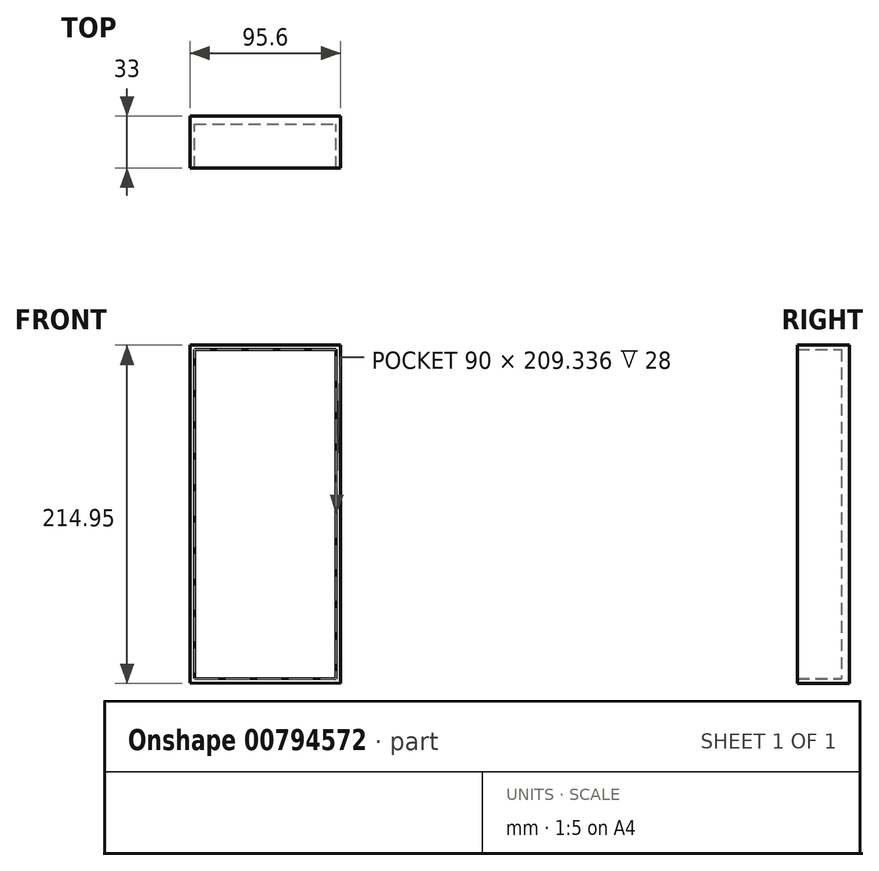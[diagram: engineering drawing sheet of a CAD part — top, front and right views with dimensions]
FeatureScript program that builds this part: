
annotation { "Feature Type Name" : "Feature", "Feature Type Description" : "" }
export const myFeature = defineFeature(function(context is Context, id is Id, definition is map)
    precondition{}
    {
        {
            var Q0;
            Q0=qCreatedBy(makeId("Front.planeOp"),FACE);
            var sketch = newSketch(context, id + "F0", { "sketchPlane" : qUnion([Q0])});
            skLineSegment(sketch, "E0", {"start": v(-49.75, 98.02) * mm, "end": v(40.25, 98.02) * mm});
            skLineSegment(sketch, "E1", {"start": v(-49.75, 98.02) * mm, "end": v(-49.75, -110.98) * mm});
            skLineSegment(sketch, "E2", {"start": v(40.25, 98.02) * mm, "end": v(40.25, -111.32) * mm});
            skLineSegment(sketch, "E3", {"start": v(-49.75, -110.98) * mm, "end": v(40.25, -111.32) * mm});
            skLineSegment(sketch, "E4.0", {"start": v(-52.55, 100.82) * mm, "end": v(43.05, 100.82) * mm});
            skLineSegment(sketch, "E4.1", {"start": v(-52.55, 100.82) * mm, "end": v(-52.55, -113.77) * mm});
            skLineSegment(sketch, "E4.2", {"start": v(-52.55, -113.77) * mm, "end": v(43.05, -114.13) * mm});
            skLineSegment(sketch, "E4.3", {"start": v(43.05, 100.82) * mm, "end": v(43.05, -114.13) * mm});
            skSolve(sketch);
        }
        {
            var Q0;
            Q0=makeQuery(id+"F0.imprint","IMPRINT",FACE,{"disambiguationData":[TD([[makeQuery(id+"F0.imprint","IMPRINT",EDGE,{"derivedFrom":sQuery(id+"F0.wireOp",EDGE,"E0")}),1.0]])]});
            extrude(context, id + "F1", {"entities" : qUnion([Q0]), "depth" : 28 * mm, "offsetDistance" : 25 * mm});
        }
        {
            var Q0;
            Q0=makeQuery(id+"F0.imprint","IMPRINT",FACE,{"disambiguationData":[TD([[makeQuery(id+"F0.imprint","IMPRINT",EDGE,{"derivedFrom":sQuery(id+"F0.wireOp",EDGE,"E0")}),-1.0]])]});
            var Q1;
            Q1=makeQuery(id+"F1.opExtrude","CAP_FACE",FACE,{"disambiguationData":[OSD([sQuery(id+"F0.wireOp",EDGE,"E0"),sQuery(id+"F0.wireOp",EDGE,"E1"),sQuery(id+"F0.wireOp",EDGE,"E2"),sQuery(id+"F0.wireOp",EDGE,"E3"),sQuery(id+"F0.wireOp",EDGE,"E4.0"),sQuery(id+"F0.wireOp",EDGE,"E4.1"),sQuery(id+"F0.wireOp",EDGE,"E4.2"),sQuery(id+"F0.wireOp",EDGE,"E4.3")])],"isStart":false});
            extrude(context, id + "F2", {"entities" : qUnion([Q0, Q1]), "operationType" : NewBodyOperationType.ADD, "depth" : 5 * mm, "offsetDistance" : 25 * mm});
        }
    });
